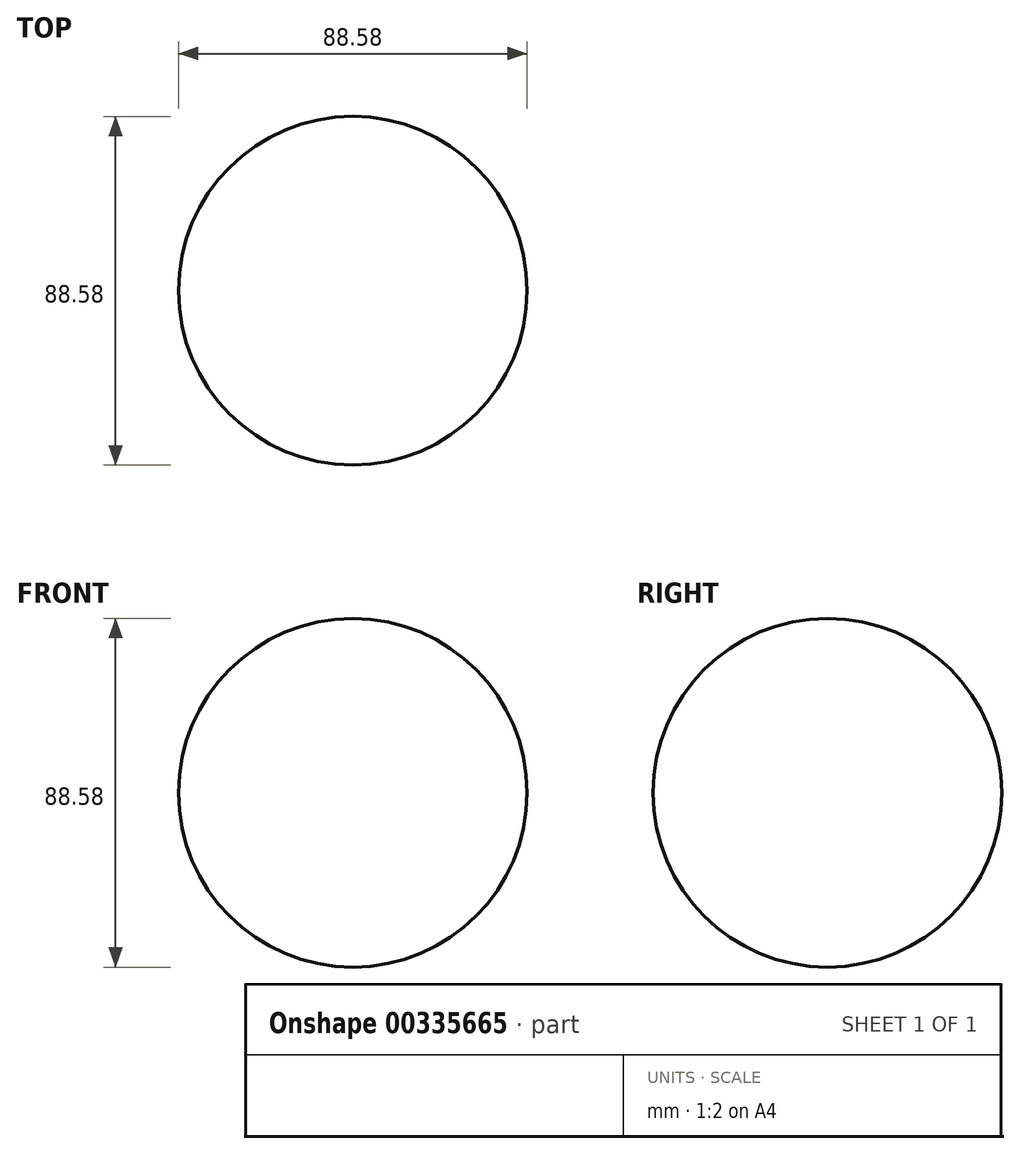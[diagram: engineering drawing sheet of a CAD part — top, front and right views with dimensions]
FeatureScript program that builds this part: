
annotation { "Feature Type Name" : "Feature", "Feature Type Description" : "" }
export const myFeature = defineFeature(function(context is Context, id is Id, definition is map)
    precondition{}
    {
        {
            var Q0;
            Q0=qCreatedBy(makeId("Front.planeOp"),FACE);
            var sketch = newSketch(context, id + "F0", { "sketchPlane" : qUnion([Q0])});
            skArc(sketch, "E0", {"start": v(0, 44.3) * mm, "mid": v(44.3, 0) * mm, "end": v(0, -44.3) * mm});
            skLineSegment(sketch, "E1", {"start": v(0, 44.3) * mm, "end": v(0, -44.3) * mm});
            skSolve(sketch);
        }
        {
            var Q0;
            Q0 = qSketchRegion(id + "F0", true);
            var Q1;
            Q1=sQuery(id+"F0.wireOp",EDGE,"E1");
            revolve(context, id + "F1", {"entities" : qUnion([Q0]), "axis" : qUnion([Q1]), "revolveType" : RevolveType.FULL});
        }
    });
